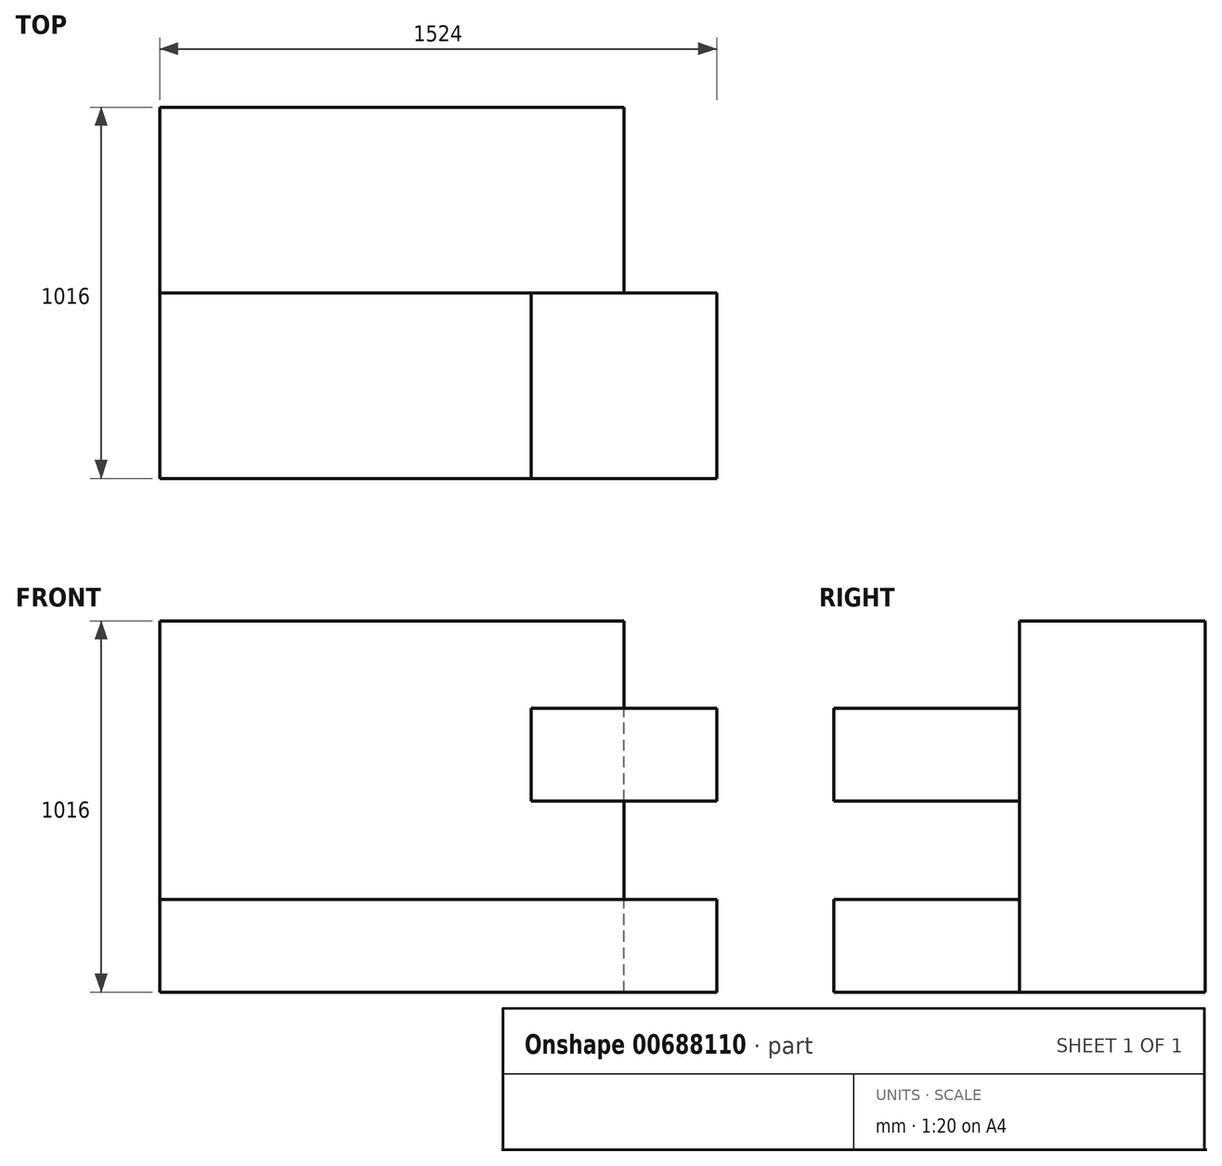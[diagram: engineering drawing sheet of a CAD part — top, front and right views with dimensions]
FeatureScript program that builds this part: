
annotation { "Feature Type Name" : "Feature", "Feature Type Description" : "" }
export const myFeature = defineFeature(function(context is Context, id is Id, definition is map)
    precondition{}
    {
        {
            var Q0;
            Q0=qCreatedBy(makeId("Front.planeOp"),FACE);
            var sketch = newSketch(context, id + "F0", { "sketchPlane" : qUnion([Q0])});
            skLineSegment(sketch, "E0.bottom", {"start": v(-780.25, 493.02) * mm, "end": v(743.75, 493.02) * mm});
            skLineSegment(sketch, "E0.top", {"start": v(-780.25, -522.98) * mm, "end": v(743.75, -522.98) * mm});
            skLineSegment(sketch, "E0.left", {"start": v(-780.25, 493.02) * mm, "end": v(-780.25, -522.98) * mm});
            skLineSegment(sketch, "E0.right", {"start": v(743.75, 493.02) * mm, "end": v(743.75, -522.98) * mm});
            skSolve(sketch);
        }
        {
            var Q0;
            Q0 = qSketchRegion(id + "F0", true);
            extrude(context, id + "F1", {"entities" : qUnion([Q0]), "depth" : 1016 * mm, "offsetDistance" : 25.4 * mm});
        }
        {
            var Q0;
            Q0=makeQuery(id+"F1.opExtrude","SWEPT_FACE",FACE,{"disambiguationData":[OSD([sQuery(id+"F0.wireOp",EDGE,"E0.bottom")])]});
            var sketch = newSketch(context, id + "F2", { "sketchPlane" : qUnion([Q0])});
            skLineSegment(sketch, "E1", {"start": v(743.75, 0) * mm, "end": v(489.75, 0) * mm});
            skLineSegment(sketch, "E2", {"start": v(489.75, 0) * mm, "end": v(489.75, -508) * mm});
            skLineSegment(sketch, "E3", {"start": v(489.75, -508) * mm, "end": v(743.75, -508) * mm});
            skSolve(sketch);
        }
        {
            var Q0;
            Q0 = qSketchRegion(id + "F2", true);
            var Q1;
            {var subQ0=sQuery(id+"F2.wireOp",EDGE,"E1");Q1=makeQuery(id+"F2.imprint","IMPRINT",FACE,{"disambiguationData":[TD([[makeQuery(id+"F2.imprint","IMPRINT",EDGE,{"derivedFrom":subQ0}),-1.0]])]});}
            extrude(context, id + "F3", {"entities" : qUnion([Q0, Q1]), "operationType" : NewBodyOperationType.REMOVE, "oppositeDirection" : true, "depth" : 1524 * mm, "offsetDistance" : 25.4 * mm});
        }
        {
            var Q0;
            Q0=makeQuery(id+"F1.opExtrude","CAP_FACE",FACE,{"disambiguationData":[OSD([sQuery(id+"F0.wireOp",EDGE,"E0.bottom"),sQuery(id+"F0.wireOp",EDGE,"E0.top"),sQuery(id+"F0.wireOp",EDGE,"E0.left"),sQuery(id+"F0.wireOp",EDGE,"E0.right")])],"isStart":false});
            var sketch = newSketch(context, id + "F4", { "sketchPlane" : qUnion([Q0])});
            skLineSegment(sketch, "E4", {"start": v(-780.25, 493.02) * mm, "end": v(-780.25, -268.98) * mm});
            skLineSegment(sketch, "E5", {"start": v(-780.25, -268.98) * mm, "end": v(743.75, -268.98) * mm});
            skLineSegment(sketch, "E6", {"start": v(743.75, -268.98) * mm, "end": v(743.75, 0) * mm});
            skLineSegment(sketch, "E7", {"start": v(743.75, 0) * mm, "end": v(235.75, 0) * mm});
            skLineSegment(sketch, "E8", {"start": v(235.75, 0) * mm, "end": v(235.75, 254) * mm});
            skLineSegment(sketch, "E9", {"start": v(235.75, 254) * mm, "end": v(743.75, 254) * mm});
            skSolve(sketch);
        }
        {
            var Q0;
            Q0 = qSketchRegion(id + "F4", true);
            var Q1;
            Q1=makeQuery(id+"F4.imprint","IMPRINT",FACE,{"disambiguationData":[TD([[makeQuery(id+"F4.imprint","IMPRINT",EDGE,{"derivedFrom":sQuery(id+"F4.wireOp",EDGE,"E4")}),1.0]])]});
            extrude(context, id + "F5", {"entities" : qUnion([Q0, Q1]), "operationType" : NewBodyOperationType.REMOVE, "oppositeDirection" : true, "depth" : 508 * mm, "offsetDistance" : 25.4 * mm});
        }
    });
